# Revit family: IS_Hotline_K2774_BIM_BE
name_source: partatom
category: Plumbing Fixtures
revit_build: Autodesk Revit 2015 (Build: 20140606_1530(x64)
units: mm (PartAtom-declared; Revit-internal decimal feet)

## types (1)
- K277401 - Hotline Plus Receveur rectangulaire 1000 x 800 mm P=65mm
    Accesoires = www.idealstandard.be
    Afwerking = Wit
    Auteur = Ideal Standard Produktions-GmbH
    Barcode = 4015413057943
    Beschrijvingdouchekop = 0
    Beschrijvinggarantie = Fabrieksgarantie
    BimObjectNaam = ISI_IdealStandard_Douche_Hotline_K277401
    Breedte = 0
    BrutoGewicht = 0
    Cost = 0 $
    Default Elevation = 0 mm  [stored 0 ft]
    Description = Hotline Plus Receveur rectangulaire 1000 x 800 mm P=65mm
    Diepte = 0 mm  [stored 0 ft]
    Dimensions = 800 x 1000 x 40 mm
    Douchebak = No
    DuurEenheid = jaar
    Eigenschappen = Hotline Plus rechthoekige douchebak 100x80  in acryl. Vervaardigd volgens DIN 14527. Met glasvezel verstevigd en ingewerkte bodem- en randversteviging. Afloopgat Ø90 mm. Potenset separaat te bestellen.
    Garantieonderdelen = 10
    GrootteAfvoergat = 0
    Hauteur = 40 mm
    IfcExportAs = IfcSanitaryTerminalType
    IfcExportType = SHOWERS
    Installatieinstructies = www.idealstandard.be
    Kleur = Wit
    Largeur = 1000 mm
    Lengte = 0 mm  [stored 0 ft]
    Longueur = 800 mm
    Manufacturer = www.idealstandard.be
    Materiaal = Acryl
    Merk = Ideal Standard
    Model = K277401
    Nettogewicht = 16
    Normen = DIN 14527
    Productinformatie = www.idealstandard.be
    Telefoonnummer = 0032 2 325 66 00
    Typeconnectie = Sanitair
    URL = www.idealstandard.be
    Uniclass2015Beschrijving = Douche
    Uniclass2015Version = Products v1.1
    Urlproducent = www.idealstandard.be
    Versie = 1
    Vervangingskosten = 0
    Verwachtelevensduur = 25 jaar
    Volumeunits = liter
    Vorm = rechthoekig

note: [stored X ft] marks values corroborated as IEEE doubles in the binary element streams (Revit-internal decimal feet)

## geometry (parser evidence)
native form markers: Blend x4, Sweep x1
no freeform markers — native parametric forms only
